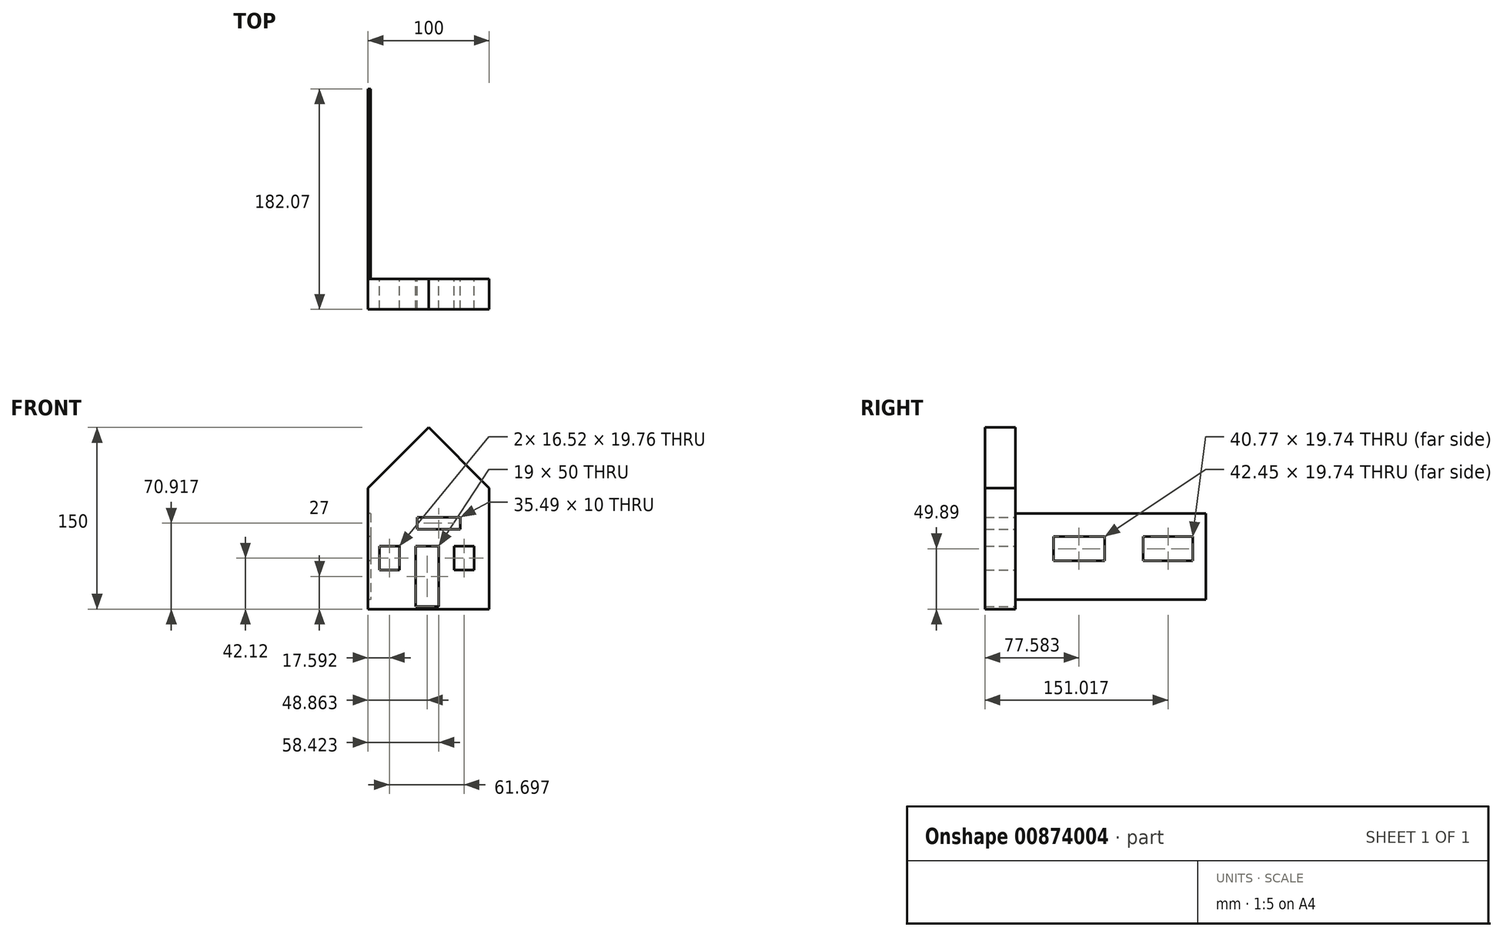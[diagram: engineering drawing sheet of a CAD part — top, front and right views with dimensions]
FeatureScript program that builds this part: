
annotation { "Feature Type Name" : "Feature", "Feature Type Description" : "" }
export const myFeature = defineFeature(function(context is Context, id is Id, definition is map)
    precondition{}
    {
        {
            var Q0;
            Q0=qCreatedBy(makeId("Top.planeOp"),FACE);
            var sketch = newSketch(context, id + "F0", { "sketchPlane" : qUnion([Q0])});
            skLineSegment(sketch, "E0.bottom", {"start": v(0, 120) * mm, "end": v(-100, 120) * mm});
            skLineSegment(sketch, "E0.top", {"start": v(0, 0) * mm, "end": v(-100, 0) * mm});
            skLineSegment(sketch, "E0.left", {"start": v(0, 120) * mm, "end": v(0, 0) * mm});
            skLineSegment(sketch, "E0.right", {"start": v(-100, 120) * mm, "end": v(-100, 0) * mm});
            skLineSegment(sketch, "E1", {"start": v(-100, 2) * mm, "end": v(0, 2) * mm});
            skLineSegment(sketch, "E2", {"start": v(-100, 118) * mm, "end": v(0, 118) * mm});
            skSolve(sketch);
        }
        {
            var Q0;
            Q0=qCreatedBy(makeId("Front.planeOp"),FACE);
            var sketch = newSketch(context, id + "F1", { "sketchPlane" : qUnion([Q0])});
            skLineSegment(sketch, "E3", {"start": v(-100, 0) * mm, "end": v(0, 0) * mm});
            skLineSegment(sketch, "E4", {"start": v(0, 0) * mm, "end": v(0, 100) * mm});
            skLineSegment(sketch, "E5", {"start": v(0, 100) * mm, "end": v(-50, 150) * mm});
            skLineSegment(sketch, "E6", {"start": v(-50, 150) * mm, "end": v(-100, 100) * mm});
            skLineSegment(sketch, "E7", {"start": v(-100, 100) * mm, "end": v(-100, 0) * mm});
            skLineSegment(sketch, "E8.bottom", {"start": v(-28.97, 52) * mm, "end": v(-12.45, 52) * mm});
            skLineSegment(sketch, "E8.top", {"start": v(-28.97, 32.24) * mm, "end": v(-12.45, 32.24) * mm});
            skLineSegment(sketch, "E8.left", {"start": v(-28.97, 52) * mm, "end": v(-28.97, 32.24) * mm});
            skLineSegment(sketch, "E8.right", {"start": v(-12.45, 52) * mm, "end": v(-12.45, 32.24) * mm});
            skLineSegment(sketch, "E9.bottom", {"start": v(-41.64, 52) * mm, "end": v(-60.64, 52) * mm});
            skLineSegment(sketch, "E9.top", {"start": v(-41.64, 2) * mm, "end": v(-60.64, 2) * mm});
            skLineSegment(sketch, "E9.left", {"start": v(-41.64, 52) * mm, "end": v(-41.64, 2) * mm});
            skLineSegment(sketch, "E9.right", {"start": v(-60.64, 52) * mm, "end": v(-60.64, 2) * mm});
            skLineSegment(sketch, "E10.bottom", {"start": v(-74.15, 52) * mm, "end": v(-90.67, 52) * mm});
            skLineSegment(sketch, "E10.top", {"start": v(-74.15, 32.24) * mm, "end": v(-90.67, 32.24) * mm});
            skLineSegment(sketch, "E10.left", {"start": v(-74.15, 52) * mm, "end": v(-74.15, 32.24) * mm});
            skLineSegment(sketch, "E10.right", {"start": v(-90.67, 52) * mm, "end": v(-90.67, 32.24) * mm});
            skLineSegment(sketch, "E11.bottom", {"start": v(-59.32, 75.92) * mm, "end": v(-23.83, 75.92) * mm});
            skLineSegment(sketch, "E11.top", {"start": v(-59.32, 65.92) * mm, "end": v(-23.83, 65.92) * mm});
            skLineSegment(sketch, "E11.left", {"start": v(-59.32, 75.92) * mm, "end": v(-59.32, 65.92) * mm});
            skLineSegment(sketch, "E11.right", {"start": v(-23.83, 75.92) * mm, "end": v(-23.83, 65.92) * mm});
            skSolve(sketch);
        }
        {
            var Q0;
            Q0 = qSketchRegion(id + "F1", true);
            extrude(context, id + "F2", {"entities" : qUnion([Q0]), "depth" : 25 * mm, "offsetDistance" : 25 * mm});
        }
        {
            var Q0;
            Q0=qCreatedBy(makeId("Right.planeOp"),FACE);
            var Q1;
            Q1=sQuery(id+"F0.wireOp",VERTEX,"E0.right.start");
            cPlane(context, id + "F3", {"entities" : qUnion([Q0, Q1]), "cplaneType" : CPlaneType.PLANE_POINT, "offset" : 25 * mm, "width" : 150 * mm, "height" : 150 * mm});
        }
        {
            var Q0;
            Q0=qCreatedBy(id+"F3.planeOp",FACE);
            var sketch = newSketch(context, id + "F4", { "sketchPlane" : qUnion([Q0])});
            skLineSegment(sketch, "E12.bottom", {"start": v(157.07, 79.07) * mm, "end": v(0, 79.07) * mm});
            skLineSegment(sketch, "E12.top", {"start": v(157.07, 7.83) * mm, "end": v(0, 7.83) * mm});
            skLineSegment(sketch, "E12.left", {"start": v(157.07, 79.07) * mm, "end": v(157.07, 7.83) * mm});
            skLineSegment(sketch, "E12.right", {"start": v(0, 79.07) * mm, "end": v(0, 7.83) * mm});
            skLineSegment(sketch, "E13.bottom", {"start": v(73.8, 59.76) * mm, "end": v(31.36, 59.76) * mm});
            skLineSegment(sketch, "E13.top", {"start": v(73.8, 40.02) * mm, "end": v(31.36, 40.02) * mm});
            skLineSegment(sketch, "E13.left", {"start": v(73.8, 59.76) * mm, "end": v(73.8, 40.02) * mm});
            skLineSegment(sketch, "E13.right", {"start": v(31.36, 59.76) * mm, "end": v(31.36, 40.02) * mm});
            skLineSegment(sketch, "E14.bottom", {"start": v(146.4, 59.76) * mm, "end": v(105.63, 59.76) * mm});
            skLineSegment(sketch, "E14.top", {"start": v(146.4, 40.02) * mm, "end": v(105.63, 40.02) * mm});
            skLineSegment(sketch, "E14.left", {"start": v(146.4, 59.76) * mm, "end": v(146.4, 40.02) * mm});
            skLineSegment(sketch, "E14.right", {"start": v(105.63, 59.76) * mm, "end": v(105.63, 40.02) * mm});
            skSolve(sketch);
        }
        {
            var Q0;
            Q0=makeQuery(id+"F4.imprint","IMPRINT",FACE,{"disambiguationData":[TD([[makeQuery(id+"F4.imprint","IMPRINT",EDGE,{"derivedFrom":sQuery(id+"F4.wireOp",EDGE,"E12.bottom")}),1.0]])]});
            extrude(context, id + "F5", {"entities" : qUnion([Q0]), "depth" : 2 * mm, "offsetDistance" : 25 * mm});
        }
    });
